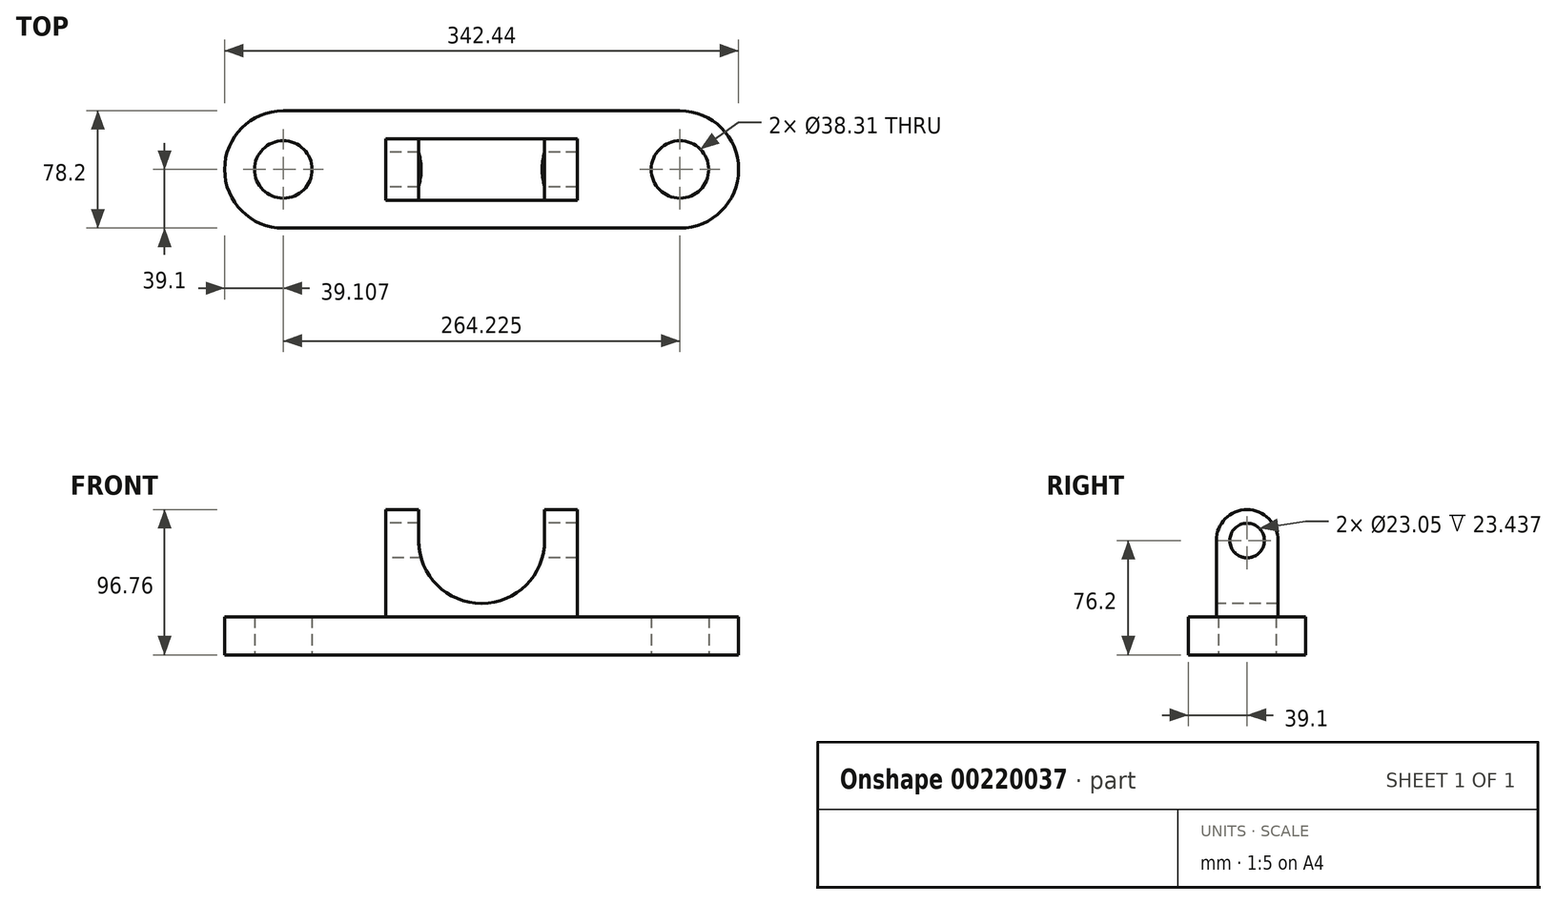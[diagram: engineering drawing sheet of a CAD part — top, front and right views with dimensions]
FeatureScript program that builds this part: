
annotation { "Feature Type Name" : "Feature", "Feature Type Description" : "" }
export const myFeature = defineFeature(function(context is Context, id is Id, definition is map)
    precondition{}
    {
        {
            var Q0;
            Q0=qCreatedBy(makeId("Top.planeOp"),FACE);
            var sketch = newSketch(context, id + "F0", { "sketchPlane" : qUnion([Q0])});
            skLineSegment(sketch, "E0.bottom", {"start": v(132.11, 39.1) * mm, "end": v(-132.11, 39.1) * mm});
            skLineSegment(sketch, "E0.top", {"start": v(132.11, -39.1) * mm, "end": v(-132.11, -39.1) * mm});
            skPoint(sketch, "E0.middle", {"position": v(0, 0) * mm});
            skArc(sketch, "E1", {"start": v(-132.11, 39.1) * mm, "mid": v(-171.22, 0) * mm, "end": v(-132.11, -39.1) * mm});
            skArc(sketch, "E2", {"start": v(132.11, -39.1) * mm, "mid": v(171.22, 0) * mm, "end": v(132.11, 39.1) * mm});
            skCircle(sketch, "E3", {"center": v(-132.11, 0) * mm, "radius": 19.16 * mm});
            skCircle(sketch, "E4.MirrorC", {"center": v(132.11, 0) * mm, "radius": 19.16 * mm});
            skSolve(sketch);
        }
        {
            var Q0;
            Q0=makeQuery(id+"F0.imprint","IMPRINT",FACE,{"disambiguationData":[TD([[makeQuery(id+"F0.imprint","IMPRINT",EDGE,{"derivedFrom":sQuery(id+"F0.wireOp",EDGE,"E0.bottom")}),1.0]])]});
            extrude(context, id + "F1", {"entities" : qUnion([Q0]), "depth" : 25.4 * mm});
        }
        {
            var Q0;
            Q0=makeQuery(id+"F1.opExtrude","CAP_FACE",FACE,{"disambiguationData":[OSD([sQuery(id+"F0.wireOp",EDGE,"E0.bottom"),sQuery(id+"F0.wireOp",EDGE,"E0.top"),sQuery(id+"F0.wireOp",EDGE,"E1"),sQuery(id+"F0.wireOp",EDGE,"E2"),sQuery(id+"F0.wireOp",EDGE,"E3"),sQuery(id+"F0.wireOp",EDGE,"E4.MirrorC")])],"isStart":false});
            var sketch = newSketch(context, id + "F2", { "sketchPlane" : qUnion([Q0])});
            skLineSegment(sketch, "E5.bottom", {"start": v(63.76, 20.56) * mm, "end": v(-63.76, 20.56) * mm});
            skLineSegment(sketch, "E5.top", {"start": v(63.76, -20.56) * mm, "end": v(-63.76, -20.56) * mm});
            skLineSegment(sketch, "E5.left", {"start": v(63.76, 20.56) * mm, "end": v(63.76, -20.56) * mm});
            skLineSegment(sketch, "E5.right", {"start": v(-63.76, 20.56) * mm, "end": v(-63.76, -20.56) * mm});
            skPoint(sketch, "E5.middle", {"position": v(0, 0) * mm});
            skSolve(sketch);
        }
        {
            var Q0;
            Q0 = qSketchRegion(id + "F2", true);
            extrude(context, id + "F3", {"entities" : qUnion([Q0]), "operationType" : NewBodyOperationType.ADD, "depth" : 50.8 * mm});
        }
        {
            var Q0;
            Q0=makeQuery(id+"F3.opExtrude","SWEPT_FACE",FACE,{"disambiguationData":[OSD([sQuery(id+"F2.wireOp",EDGE,"E5.top")])]});
            var sketch = newSketch(context, id + "F4", { "sketchPlane" : qUnion([Q0])});
            skCircle(sketch, "E6", {"center": v(0, 76.2) * mm, "radius": 41.94 * mm});
            skSolve(sketch);
        }
        {
            var Q0;
            {var subQ0=sQuery(id+"F4.wireOp",EDGE,"E6");var subQ1=makeQuery(id+"F3.opExtrude","CAP_EDGE",EDGE,{"disambiguationData":[OSD([sQuery(id+"F2.wireOp",EDGE,"E5.top")])],"isStart":false});var subQ2=makeQuery(id+"F4.imprint","INTERSECT",VERTEX,{"disambiguationData":[OD(0.0)],"derivedFrom":[subQ1,subQ0]});Q0=makeQuery(id+"F4.imprint","IMPRINT",FACE,{"disambiguationData":[TD([[makeQuery(id+"F4.imprint","IMPRINT",EDGE,{"disambiguationData":[TD([[subQ2,1.0]])],"derivedFrom":subQ0}),1.0]])]});}
            extrude(context, id + "F5", {"entities" : qUnion([Q0]), "operationType" : NewBodyOperationType.REMOVE, "endBound" : BoundingType.THROUGH_ALL, "oppositeDirection" : true, "depth" : 25.4 * mm});
        }
        {
            var Q0;
            Q0=makeQuery(id+"F3.opExtrude","SWEPT_FACE",FACE,{"disambiguationData":[OSD([sQuery(id+"F2.wireOp",EDGE,"E5.right")])]});
            var sketch = newSketch(context, id + "F6", { "sketchPlane" : qUnion([Q0])});
            skArc(sketch, "E7", {"start": v(20.56, 76.2) * mm, "mid": v(0, 96.76) * mm, "end": v(-20.56, 76.2) * mm});
            skSolve(sketch);
        }
        {
            var Q0;
            Q0=makeQuery(id+"F6.imprint","IMPRINT",FACE,{"disambiguationData":[TD([[makeQuery(id+"F6.imprint","IMPRINT",EDGE,{"derivedFrom":sQuery(id+"F6.wireOp",EDGE,"E7")}),1.0]])]});
            var Q1;
            {var subQ0=sQuery(id+"F4.wireOp",EDGE,"E6");var subQ1=sQuery(id+"F2.wireOp",EDGE,"E5.top");Q1=makeQuery(id+"F5.boolean.opBoolean","COPY",VERTEX,{"derivedFrom":makeQuery(id+"F5.opExtrude","CAP_VERTEX",VERTEX,{"disambiguationData":[OSD([subQ1,subQ0]),TDD([makeQuery(id+"F4.imprint","INTERSECT",VERTEX,{"disambiguationData":[OD(1.0)],"derivedFrom":[makeQuery(id+"F3.opExtrude","CAP_EDGE",EDGE,{"disambiguationData":[OSD([subQ1])],"isStart":false}),subQ0]})])],"isStart":true})});}
            extrude(context, id + "F7", {"entities" : qUnion([Q0]), "operationType" : NewBodyOperationType.ADD, "endBound" : BoundingType.UP_TO_VERTEX, "oppositeDirection" : true, "endBoundEntityVertex" : qUnion([Q1]), "depth" : 25.4 * mm});
        }
        {
            var Q0;
            {var subQ0=sQuery(id+"F2.wireOp",EDGE,"E5.right");Q0=makeQuery(id+"F7.boolean.opBoolean","MERGE",FACE,{"derivedFrom":[makeQuery(id+"F3.opExtrude","SWEPT_FACE",FACE,{"disambiguationData":[OSD([subQ0])]}),makeQuery(id+"F7.opExtrude","CAP_FACE",FACE,{"disambiguationData":[OSD([subQ0,sQuery(id+"F6.wireOp",EDGE,"E7")])],"isStart":true})]});}
            var sketch = newSketch(context, id + "F8", { "sketchPlane" : qUnion([Q0])});
            skCircle(sketch, "E8", {"center": v(0, 76.2) * mm, "radius": 11.53 * mm});
            skSolve(sketch);
        }
        {
            var Q0;
            Q0=makeQuery(id+"F8.imprint","IMPRINT",FACE,{"disambiguationData":[TD([[makeQuery(id+"F8.imprint","IMPRINT",EDGE,{"derivedFrom":sQuery(id+"F8.wireOp",EDGE,"E8")}),1.0]])]});
            var Q1;
            Q1=sQuery(id+"F8.wireOp",EDGE,"E8");
            extrude(context, id + "F9", {"entities" : qUnion([Q0]), "operationType" : NewBodyOperationType.REMOVE, "surfaceEntities" : qUnion([Q1]), "endBound" : BoundingType.THROUGH_ALL, "oppositeDirection" : true, "depth" : 25.4 * mm});
        }
        {
            var Q0;
            Q0=makeQuery(id+"F3.opExtrude","SWEPT_FACE",FACE,{"disambiguationData":[OSD([sQuery(id+"F2.wireOp",EDGE,"E5.left")])]});
            var sketch = newSketch(context, id + "F10", { "sketchPlane" : qUnion([Q0])});
            skArc(sketch, "E9.0", {"start": v(-20.56, 76.2) * mm, "mid": v(0, 96.76) * mm, "end": v(20.56, 76.2) * mm});
            skArc(sketch, "E10.0", {"start": v(11.53, 76.2) * mm, "mid": v(0, 87.73) * mm, "end": v(-11.53, 76.2) * mm});
            skPoint(sketch, "E11.0", {"position": v(-16.04, 76.2) * mm});
            skLineSegment(sketch, "E12.0", {"start": v(-11.53, 76.2) * mm, "end": v(-20.56, 76.2) * mm});
            skLineSegment(sketch, "E13.0", {"start": v(20.56, 76.2) * mm, "end": v(11.53, 76.2) * mm});
            skSolve(sketch);
        }
        {
            var Q0;
            Q0 = qSketchRegion(id + "F10", true);
            var Q1;
            Q1=makeQuery(id+"F5.boolean.opBoolean","INTERSECT",VERTEX,{"disambiguationData":[OD(0.0)],"derivedFrom":[makeQuery(id+"F3.opExtrude","SWEPT_FACE",FACE,{"disambiguationData":[OSD([sQuery(id+"F2.wireOp",EDGE,"E5.bottom")])]}),makeQuery(id+"F5.opExtrude","SWEPT_FACE",FACE,{"disambiguationData":[OSD([sQuery(id+"F4.wireOp",EDGE,"E6")])]})]});
            extrude(context, id + "F11", {"entities" : qUnion([Q0]), "operationType" : NewBodyOperationType.ADD, "endBound" : BoundingType.UP_TO_VERTEX, "oppositeDirection" : true, "endBoundEntityVertex" : qUnion([Q1]), "depth" : 25.4 * mm});
        }
    });
